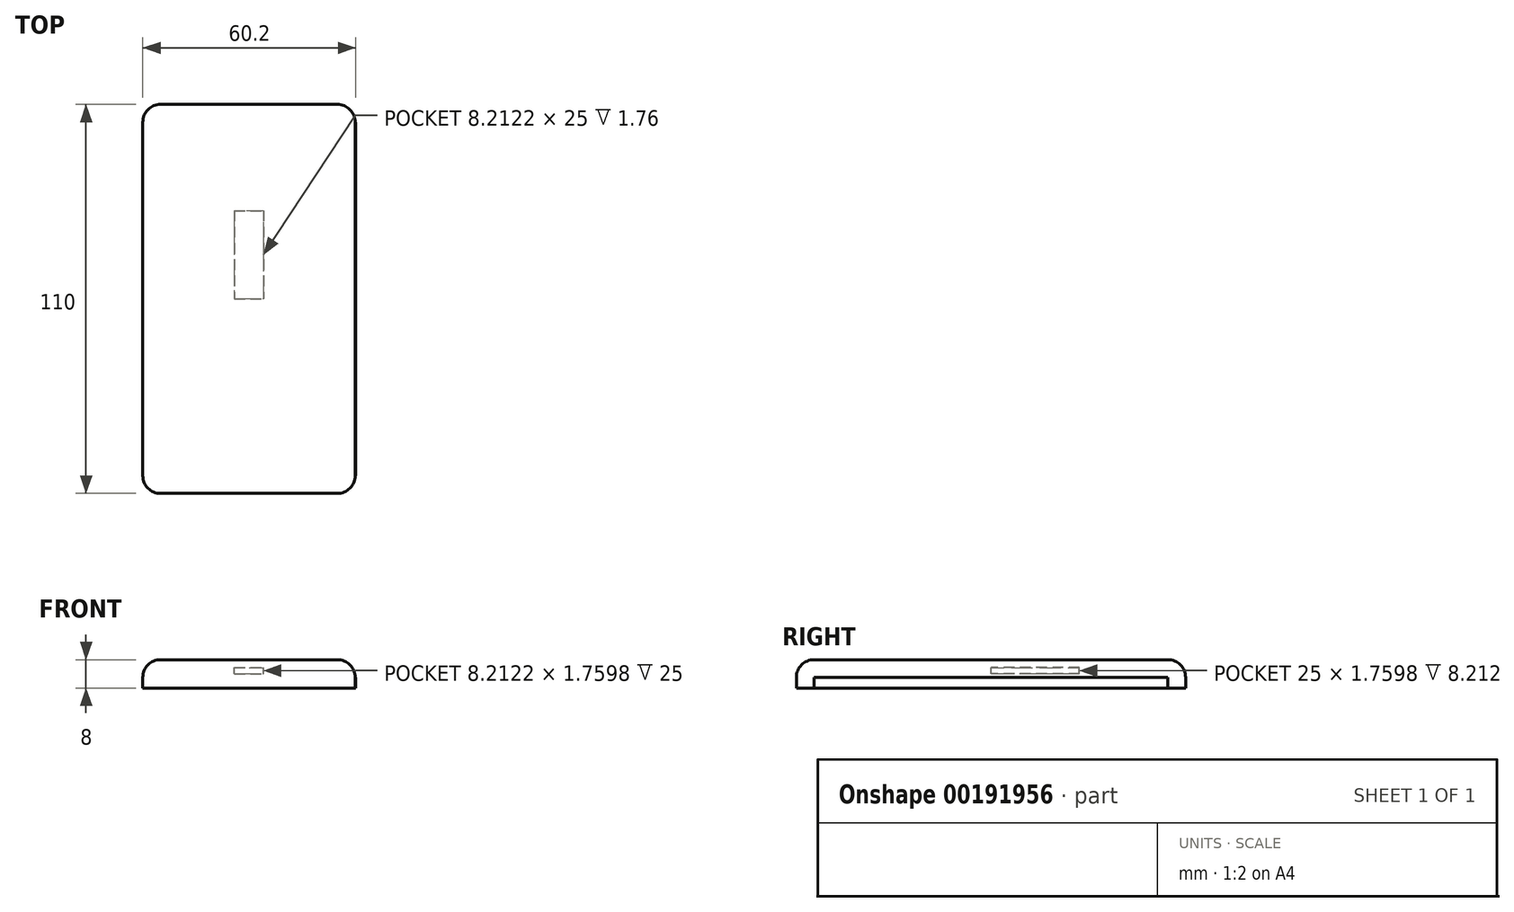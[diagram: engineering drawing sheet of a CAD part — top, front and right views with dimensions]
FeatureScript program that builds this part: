
annotation { "Feature Type Name" : "Feature", "Feature Type Description" : "" }
export const myFeature = defineFeature(function(context is Context, id is Id, definition is map)
    precondition{}
    {
        {
            var Q0;
            Q0=qCreatedBy(makeId("Top.planeOp"),FACE);
            var sketch = newSketch(context, id + "F0", { "sketchPlane" : qUnion([Q0])});
            skLineSegment(sketch, "E0.bottom", {"start": v(30, -55) * mm, "end": v(-30, -55) * mm});
            skLineSegment(sketch, "E0.top", {"start": v(30, 55) * mm, "end": v(-30, 55) * mm});
            skLineSegment(sketch, "E0.left", {"start": v(30, -55) * mm, "end": v(30, 55) * mm});
            skLineSegment(sketch, "E0.right", {"start": v(-30, -55) * mm, "end": v(-30, 55) * mm});
            skPoint(sketch, "E0.middle", {"position": v(0, 0) * mm});
            skSolve(sketch);
        }
        {
            var Q0;
            Q0=makeQuery(id+"F0.imprint","IMPRINT",FACE,{"disambiguationData":[TD([[makeQuery(id+"F0.imprint","IMPRINT",EDGE,{"derivedFrom":sQuery(id+"F0.wireOp",EDGE,"E0.bottom")}),-1.0]])]});
            extrude(context, id + "F1", {"entities" : qUnion([Q0]), "depth" : 8 * mm});
        }
        {
            var Q0;
            Q0=makeQuery(id+"F1.opExtrude","CAP_EDGE",EDGE,{"disambiguationData":[OSD([sQuery(id+"F0.wireOp",EDGE,"E0.bottom")])],"isStart":false});
            fillet(context, id + "F2", {"entities" : qUnion([Q0]), "radius" : 5 * mm, "tangentPropagation" : true, "allowEdgeOverflow" : false});
        }
        {
            var Q0;
            Q0=makeQuery(id+"F1.opExtrude","CAP_EDGE",EDGE,{"disambiguationData":[OSD([sQuery(id+"F0.wireOp",EDGE,"E0.left")])],"isStart":false});
            fillet(context, id + "F3", {"entities" : qUnion([Q0]), "radius" : 5 * mm, "tangentPropagation" : true, "allowEdgeOverflow" : false});
        }
        {
            var Q0;
            Q0=makeQuery(id+"F1.opExtrude","CAP_EDGE",EDGE,{"disambiguationData":[OSD([sQuery(id+"F0.wireOp",EDGE,"E0.top")])],"isStart":false});
            fillet(context, id + "F4", {"entities" : qUnion([Q0]), "radius" : 5 * mm, "tangentPropagation" : true, "allowEdgeOverflow" : false});
        }
        {
            var Q0;
            Q0=makeQuery(id+"F1.opExtrude","SWEPT_FACE",FACE,{"disambiguationData":[OSD([sQuery(id+"F0.wireOp",EDGE,"E0.left")])]});
            extrude(context, id + "F5", {"entities" : qUnion([Q0]), "operationType" : NewBodyOperationType.ADD, "depth" : 0.2 * mm});
        }
        {
            var Q0;
            Q0=makeQuery(id+"F1.opExtrude","CAP_EDGE",EDGE,{"disambiguationData":[OSD([sQuery(id+"F0.wireOp",EDGE,"E0.right")])],"isStart":false});
            fillet(context, id + "F6", {"entities" : qUnion([Q0]), "radius" : 5 * mm, "tangentPropagation" : true, "allowEdgeOverflow" : false});
        }
        {
            var Q0;
            Q0=qCreatedBy(makeId("Front.planeOp"),FACE);
            var sketch = newSketch(context, id + "F7", { "sketchPlane" : qUnion([Q0])});
            skLineSegment(sketch, "E1.bottom", {"start": v(-4.1, 3.96) * mm, "end": v(4.1, 3.96) * mm});
            skLineSegment(sketch, "E1.top", {"start": v(-4.1, 5.72) * mm, "end": v(4.1, 5.72) * mm});
            skLineSegment(sketch, "E1.left", {"start": v(-4.1, 3.96) * mm, "end": v(-4.1, 5.72) * mm});
            skLineSegment(sketch, "E1.right", {"start": v(4.1, 3.96) * mm, "end": v(4.1, 5.72) * mm});
            skPoint(sketch, "E1.middle", {"position": v(0, 4.84) * mm});
            skSolve(sketch);
        }
        {
            var Q0;
            Q0 = qSketchRegion(id + "F7", true);
            extrude(context, id + "F8", {"entities" : qUnion([Q0]), "operationType" : NewBodyOperationType.REMOVE, "oppositeDirection" : true, "depth" : 0.8 * mm});
        }
        {
            var Q0;
            Q0 = qSketchRegion(id + "F7", true);
            extrude(context, id + "F9", {"entities" : qUnion([Q0]), "operationType" : NewBodyOperationType.REMOVE, "oppositeDirection" : true, "depth" : 25 * mm});
        }
    });
